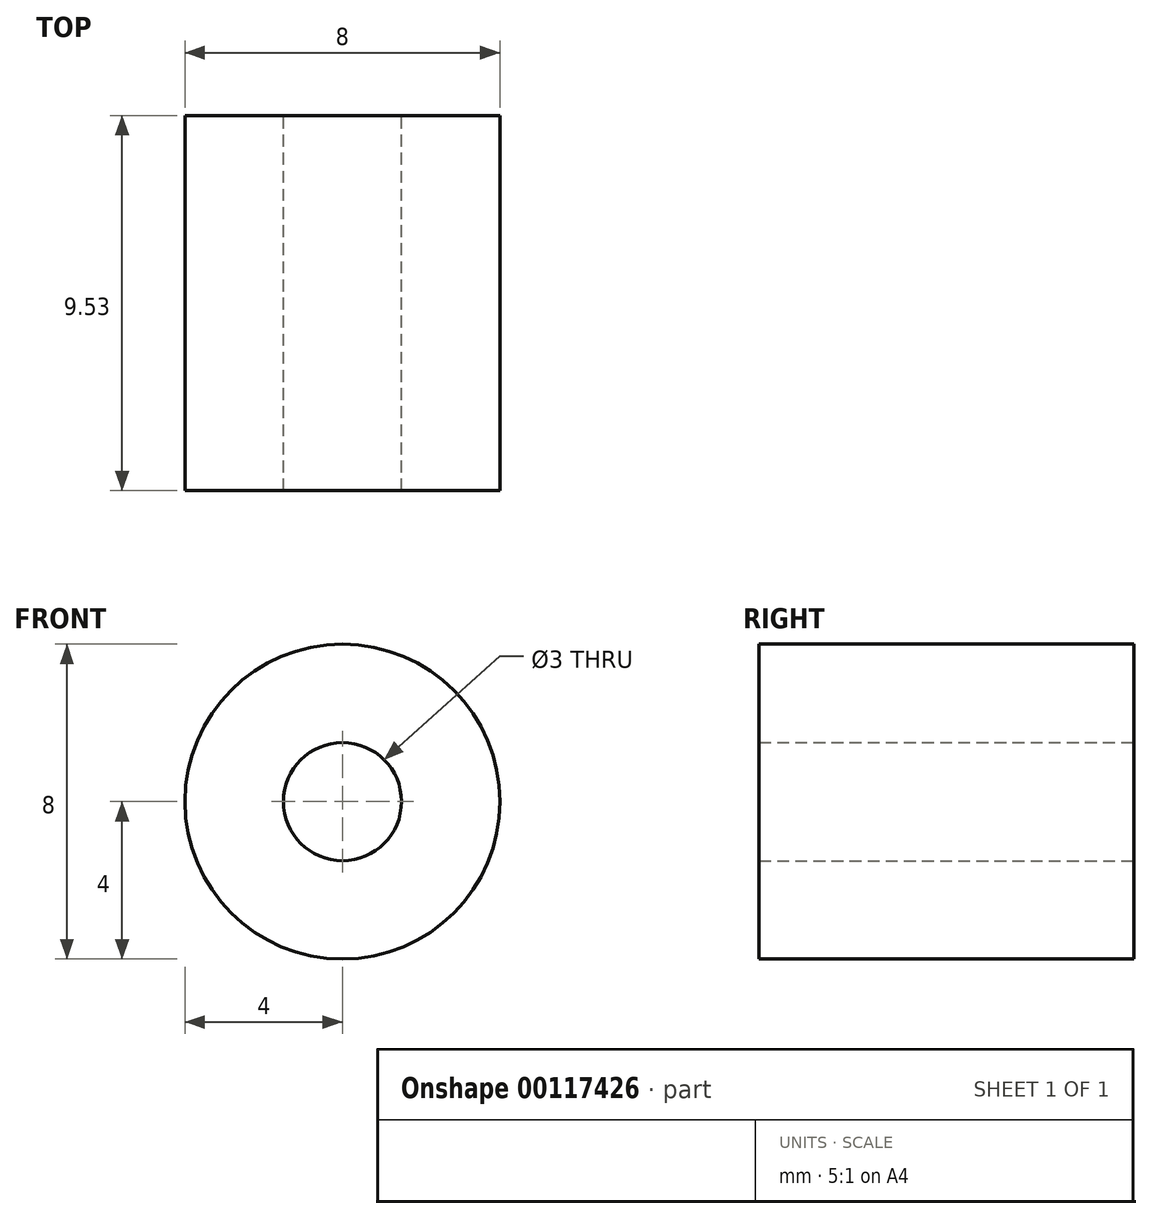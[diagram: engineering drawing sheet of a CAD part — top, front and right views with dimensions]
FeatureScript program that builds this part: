
annotation { "Feature Type Name" : "Feature", "Feature Type Description" : "" }
export const myFeature = defineFeature(function(context is Context, id is Id, definition is map)
    precondition{}
    {
        {
            var Q0;
            Q0=qCreatedBy(makeId("Front.planeOp"),FACE);
            var sketch = newSketch(context, id + "F0", { "sketchPlane" : qUnion([Q0])});
            skCircle(sketch, "E0", {"center": v(0, 0) * mm, "radius": 4 * mm});
            skCircle(sketch, "E1", {"center": v(0, 0) * mm, "radius": 1.5 * mm});
            skSolve(sketch);
        }
        {
            var Q0;
            Q0=makeQuery(id+"F0.imprint","IMPRINT",FACE,{"disambiguationData":[TD([[makeQuery(id+"F0.imprint","IMPRINT",EDGE,{"derivedFrom":sQuery(id+"F0.wireOp",EDGE,"E0")}),1.0]])]});
            var Q1;
            Q1=sQuery(id+"F0.wireOp",EDGE,"E1");
            var Q2;
            Q2=sQuery(id+"F0.wireOp",EDGE,"E0");
            extrude(context, id + "F1", {"entities" : qUnion([Q0]), "surfaceEntities" : qUnion([Q1, Q2]), "depth" : 9.52 * mm});
        }
    });
